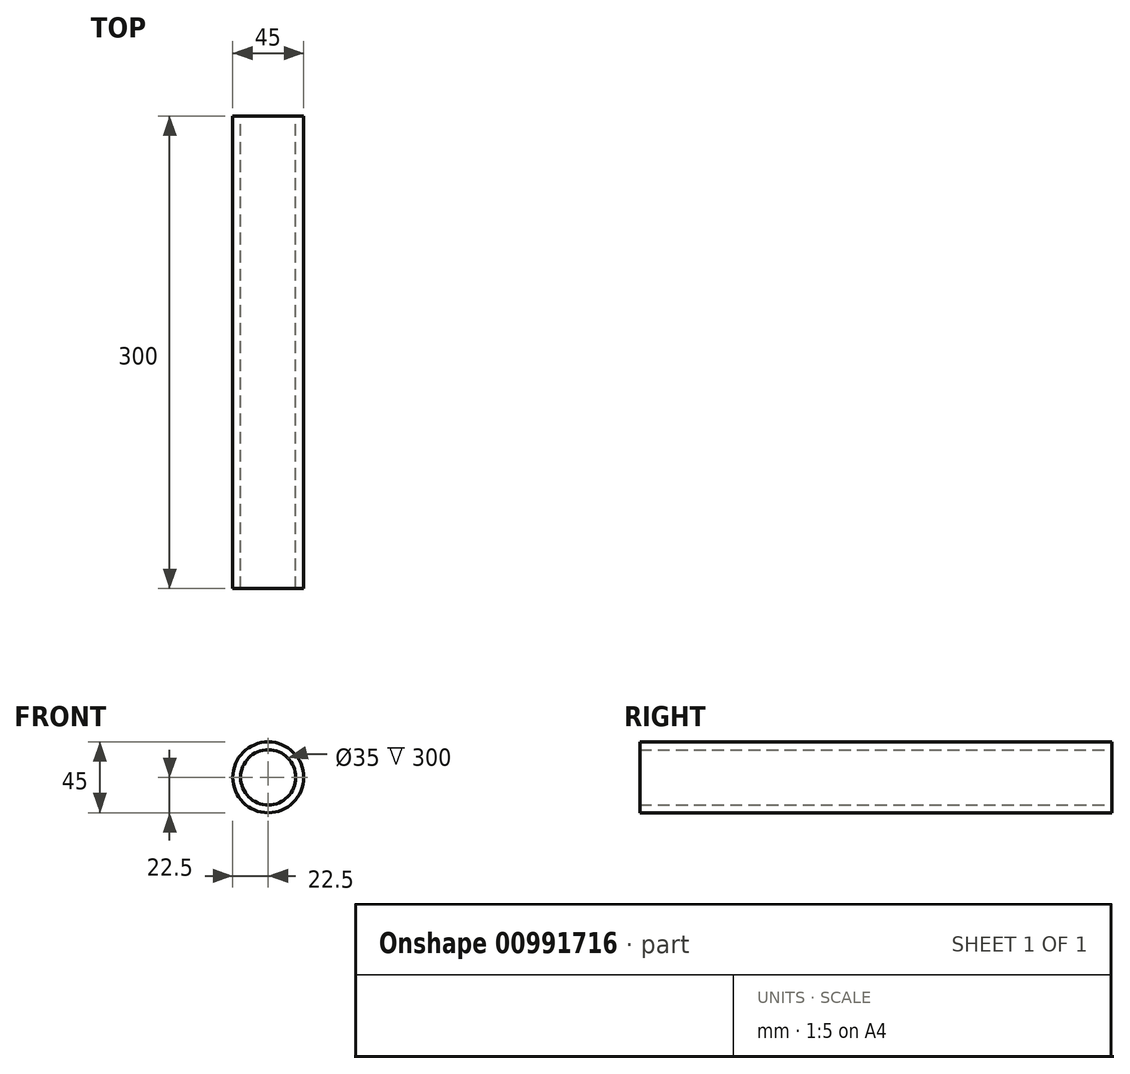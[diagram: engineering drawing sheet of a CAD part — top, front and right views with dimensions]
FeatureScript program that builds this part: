
annotation { "Feature Type Name" : "Feature", "Feature Type Description" : "" }
export const myFeature = defineFeature(function(context is Context, id is Id, definition is map)
    precondition{}
    {
        {
            var Q0;
            Q0=qCreatedBy(makeId("Front.planeOp"),FACE);
            var sketch = newSketch(context, id + "F0", { "sketchPlane" : qUnion([Q0])});
            skCircle(sketch, "E0", {"center": v(0, 0) * mm, "radius": 22.5 * mm});
            skCircle(sketch, "E1", {"center": v(0, 0) * mm, "radius": 17.5 * mm});
            skSolve(sketch);
        }
        {
            var Q0;
            Q0=makeQuery(id+"F0.imprint","IMPRINT",FACE,{"disambiguationData":[TD([[makeQuery(id+"F0.imprint","IMPRINT",EDGE,{"derivedFrom":sQuery(id+"F0.wireOp",EDGE,"E0")}),1.0]])]});
            extrude(context, id + "F1", {"entities" : qUnion([Q0]), "depth" : 300 * mm, "offsetDistance" : 25 * mm});
        }
    });
